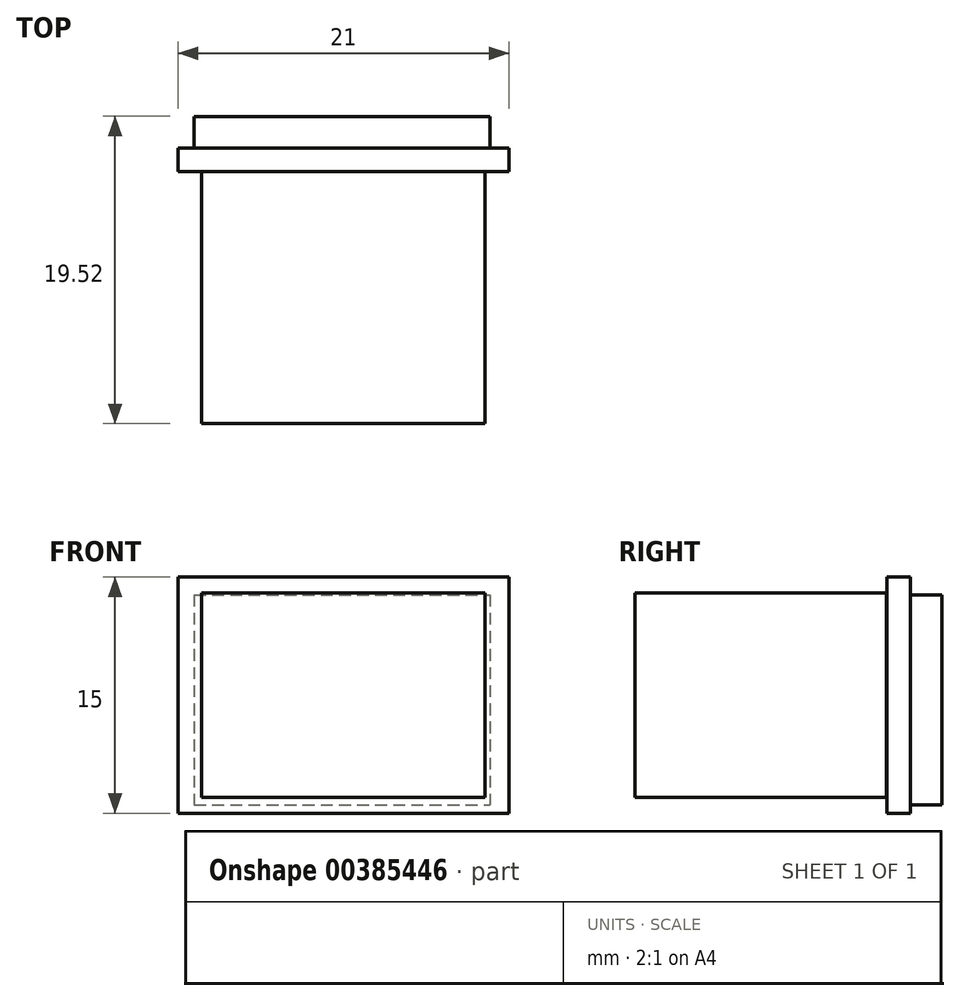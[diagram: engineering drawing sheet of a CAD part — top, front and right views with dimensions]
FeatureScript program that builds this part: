
annotation { "Feature Type Name" : "Feature", "Feature Type Description" : "" }
export const myFeature = defineFeature(function(context is Context, id is Id, definition is map)
    precondition{}
    {
        {
            var Q0;
            Q0=qCreatedBy(makeId("Top.planeOp"),FACE);
            var sketch = newSketch(context, id + "F0", { "sketchPlane" : qUnion([Q0])});
            skLineSegment(sketch, "E0.bottom", {"start": v(9, -8) * mm, "end": v(-9, -8) * mm});
            skLineSegment(sketch, "E0.top", {"start": v(9, 8) * mm, "end": v(-9, 8) * mm});
            skLineSegment(sketch, "E0.left", {"start": v(9, -8) * mm, "end": v(9, 8) * mm});
            skLineSegment(sketch, "E0.right", {"start": v(-9, -8) * mm, "end": v(-9, 8) * mm});
            skPoint(sketch, "E0.middle", {"position": v(0, 0) * mm});
            skLineSegment(sketch, "E1.bottom", {"start": v(10.5, 8) * mm, "end": v(-10.5, 8) * mm});
            skLineSegment(sketch, "E1.top", {"start": v(10.5, 9.5) * mm, "end": v(-10.5, 9.5) * mm});
            skLineSegment(sketch, "E1.left", {"start": v(10.5, 8) * mm, "end": v(10.5, 9.5) * mm});
            skLineSegment(sketch, "E1.right", {"start": v(-10.5, 8) * mm, "end": v(-10.5, 9.5) * mm});
            skPoint(sketch, "E1.middle", {"position": v(0, 8.75) * mm});
            skPoint(sketch, "E2", {"position": v(0, 8) * mm});
            skSolve(sketch);
        }
        {
            var Q0;
            {var subQ0=sQuery(id+"F0.wireOp",EDGE,"E0.bottom");Q0=makeQuery(id+"F0.imprint","IMPRINT",FACE,{"disambiguationData":[TD([[makeQuery(id+"F0.imprint","IMPRINT",EDGE,{"derivedFrom":subQ0}),-1.0]])]});}
            extrude(context, id + "F1", {"entities" : qUnion([Q0]), "depth" : 13 * mm});
        }
        {
            var Q0;
            Q0=qCreatedBy(makeId("Top.planeOp"),FACE);
            var sketch = newSketch(context, id + "F2", { "sketchPlane" : qUnion([Q0])});
            skLineSegment(sketch, "E3.bottom", {"start": v(10.5, 8.02) * mm, "end": v(-10.5, 8.02) * mm});
            skLineSegment(sketch, "E3.top", {"start": v(10.5, 9.52) * mm, "end": v(-10.5, 9.52) * mm});
            skLineSegment(sketch, "E3.left", {"start": v(10.5, 8.02) * mm, "end": v(10.5, 9.52) * mm});
            skLineSegment(sketch, "E3.right", {"start": v(-10.5, 8.02) * mm, "end": v(-10.5, 9.52) * mm});
            skPoint(sketch, "E3.middle", {"position": v(0, 8.77) * mm});
            skSolve(sketch);
        }
        {
            var Q0;
            Q0=makeQuery(id+"F2.imprint","IMPRINT",FACE,{"disambiguationData":[TD([[makeQuery(id+"F2.imprint","IMPRINT",EDGE,{"derivedFrom":sQuery(id+"F2.wireOp",EDGE,"E3.bottom")}),-1.0]])]});
            extrude(context, id + "F3", {"entities" : qUnion([Q0]), "operationType" : NewBodyOperationType.ADD, "depth" : 14 * mm, "hasSecondDirection" : true, "secondDirectionOppositeDirection" : true, "secondDirectionDepth" : 1 * mm});
        }
        {
            var Q0;
            Q0=makeQuery(id+"F3.opExtrude","SWEPT_FACE",FACE,{"disambiguationData":[OSD([sQuery(id+"F2.wireOp",EDGE,"E3.top")])]});
            var sketch = newSketch(context, id + "F4", { "sketchPlane" : qUnion([Q0])});
            skLineSegment(sketch, "E4.bottom", {"start": v(9.48, 12.88) * mm, "end": v(-9.31, 12.88) * mm});
            skLineSegment(sketch, "E4.top", {"start": v(9.48, -0.46) * mm, "end": v(-9.31, -0.46) * mm});
            skLineSegment(sketch, "E4.left", {"start": v(9.48, 12.88) * mm, "end": v(9.48, -0.46) * mm});
            skLineSegment(sketch, "E4.right", {"start": v(-9.31, 12.88) * mm, "end": v(-9.31, -0.46) * mm});
            skSolve(sketch);
        }
        {
            var Q0;
            Q0=makeQuery(id+"F4.imprint","IMPRINT",FACE,{"disambiguationData":[TD([[makeQuery(id+"F4.imprint","IMPRINT",EDGE,{"derivedFrom":sQuery(id+"F4.wireOp",EDGE,"E4.bottom")}),1.0]])]});
            extrude(context, id + "F5", {"entities" : qUnion([Q0]), "operationType" : NewBodyOperationType.ADD, "depth" : 2 * mm});
        }
    });
